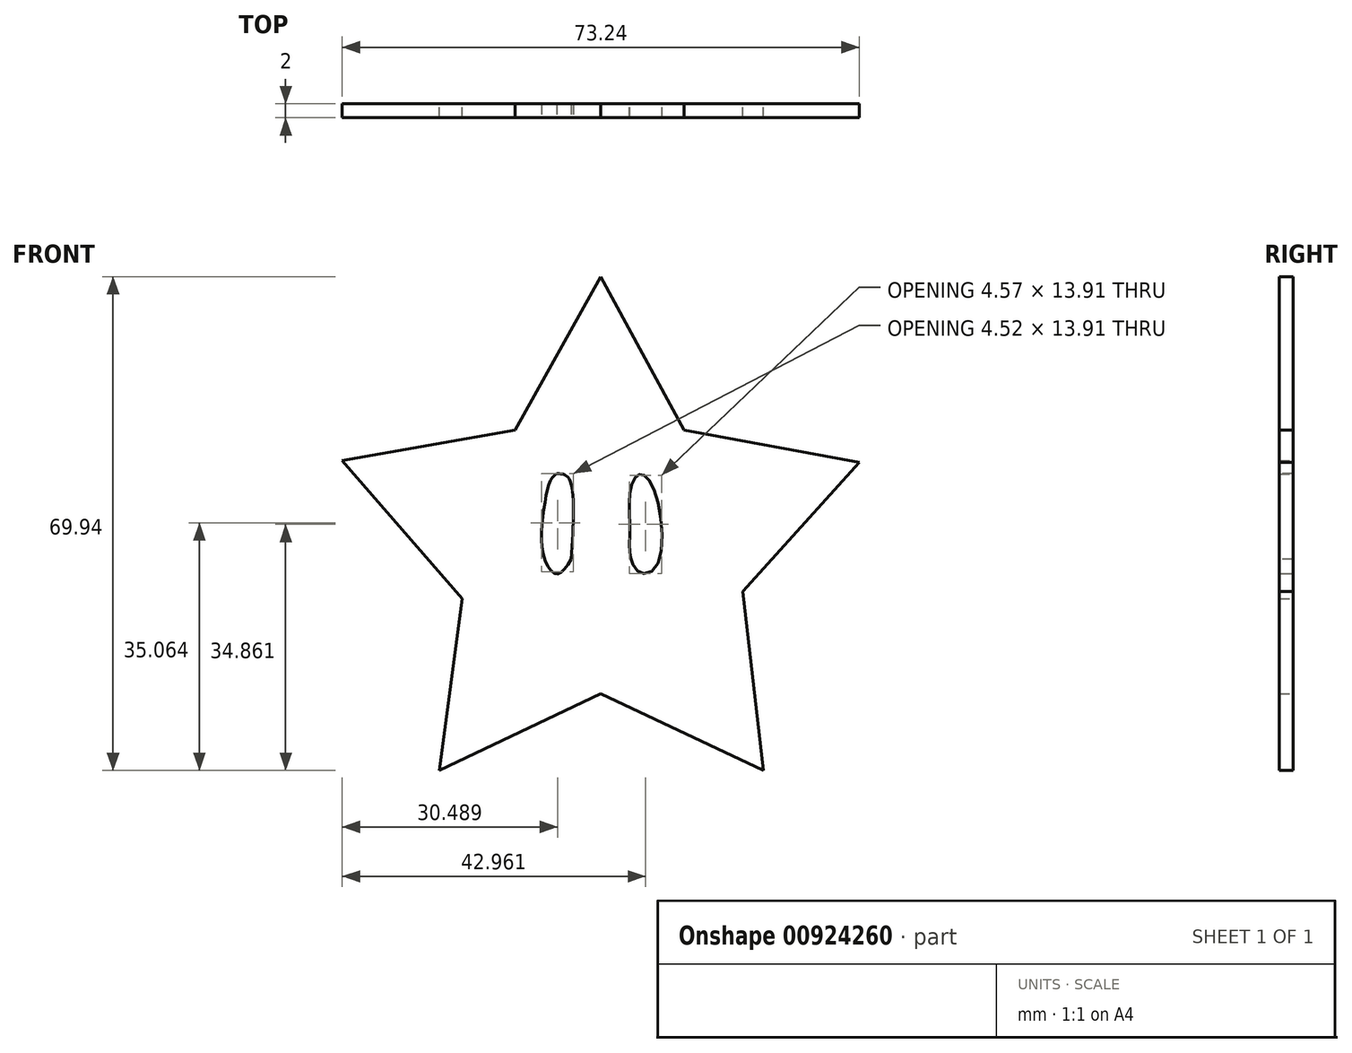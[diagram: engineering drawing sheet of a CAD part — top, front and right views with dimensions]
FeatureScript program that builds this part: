
annotation { "Feature Type Name" : "Feature", "Feature Type Description" : "" }
export const myFeature = defineFeature(function(context is Context, id is Id, definition is map)
    precondition{}
    {
        {
            var Q0;
            Q0=qCreatedBy(makeId("Front.planeOp"),FACE);
            var sketch = newSketch(context, id + "F0", { "sketchPlane" : qUnion([Q0])});
            skLineSegment(sketch, "E0", {"start": v(-73.24, 43.9) * mm, "end": v(-48.73, 48.2) * mm});
            skLineSegment(sketch, "E1", {"start": v(-48.73, 48.2) * mm, "end": v(-36.62, 69.94) * mm});
            skLineSegment(sketch, "E2", {"start": v(-36.62, 69.94) * mm, "end": v(-24.84, 48.2) * mm});
            skLineSegment(sketch, "E3", {"start": v(-24.84, 48.2) * mm, "end": v(0, 43.63) * mm});
            skLineSegment(sketch, "E4", {"start": v(0, 43.63) * mm, "end": v(-16.51, 25.37) * mm});
            skLineSegment(sketch, "E5", {"start": v(-16.51, 25.37) * mm, "end": v(-13.56, 0) * mm});
            skLineSegment(sketch, "E6", {"start": v(-13.56, 0) * mm, "end": v(-36.62, 10.87) * mm});
            skLineSegment(sketch, "E7", {"start": v(-59.47, 0) * mm, "end": v(-36.62, 10.87) * mm});
            skLineSegment(sketch, "E8", {"start": v(-59.47, 0) * mm, "end": v(-56.25, 24.3) * mm});
            skLineSegment(sketch, "E9", {"start": v(-56.25, 24.3) * mm, "end": v(-73.24, 43.9) * mm});
            skSolve(sketch);
        }
        {
            var Q0;
            Q0=makeQuery(id+"F0.imprint","IMPRINT",FACE,{"disambiguationData":[TD([[makeQuery(id+"F0.imprint","IMPRINT",EDGE,{"derivedFrom":sQuery(id+"F0.wireOp",EDGE,"E0")}),-1.0]])]});
            extrude(context, id + "F1", {"entities" : qUnion([Q0]), "depth" : 2 * mm, "offsetDistance" : 25.4 * mm});
        }
        {
            var Q0;
            Q0=makeQuery(id+"F1.opExtrude","CAP_FACE",FACE,{"disambiguationData":[OSD([sQuery(id+"F0.wireOp",EDGE,"E0"),sQuery(id+"F0.wireOp",EDGE,"E1"),sQuery(id+"F0.wireOp",EDGE,"E2"),sQuery(id+"F0.wireOp",EDGE,"E3"),sQuery(id+"F0.wireOp",EDGE,"E4"),sQuery(id+"F0.wireOp",EDGE,"E5"),sQuery(id+"F0.wireOp",EDGE,"E6"),sQuery(id+"F0.wireOp",EDGE,"E7"),sQuery(id+"F0.wireOp",EDGE,"E8"),sQuery(id+"F0.wireOp",EDGE,"E9")])],"isStart":false});
            var sketch = newSketch(context, id + "F2", { "sketchPlane" : qUnion([Q0])});
            skFitSpline(sketch, "E10", {"points": [v(-42.82, 42.02) * mm, v(-41.2, 41.47) * mm, v(-40.82, 29.9) * mm], "startDerivative": vector(6.57, -0.03) * mm, "endDerivative": vector(-1.38, -21.1) * mm});
            skFitSpline(sketch, "E11", {"points": [v(-42.82, 42.02) * mm, v(-43.66, 41.2) * mm, v(-44.63, 37.26) * mm, v(-44.7, 30.34) * mm, v(-42.82, 27.82) * mm, v(-40.82, 29.9) * mm], "startDerivative": vector(-7.6, -5.15) * mm, "endDerivative": vector(10.67, 16.83) * mm});
            skFitSpline(sketch, "E12", {"points": [v(-30.47, 41.82) * mm, v(-31.37, 41.82) * mm, v(-32.4, 39.92) * mm, v(-32.54, 35.78) * mm, v(-32.54, 31.57) * mm, v(-32.34, 29.9) * mm, v(-31.11, 28.01) * mm, v(-28.78, 28.86) * mm, v(-28.53, 37.98) * mm, v(-30.47, 41.82) * mm]});
            skSolve(sketch);
        }
        {
            var Q0;
            Q0=makeQuery(id+"F2.imprint","IMPRINT",FACE,{"disambiguationData":[TD([[makeQuery(id+"F2.imprint","IMPRINT",EDGE,{"derivedFrom":sQuery(id+"F2.wireOp",EDGE,"E10")}),-1.0]])]});
            var Q1;
            Q1=makeQuery(id+"F2.imprint","IMPRINT",FACE,{"disambiguationData":[TD([[makeQuery(id+"F2.imprint","IMPRINT",EDGE,{"derivedFrom":sQuery(id+"F2.wireOp",EDGE,"E12")}),1.0]])]});
            extrude(context, id + "F3", {"entities" : qUnion([Q0, Q1]), "operationType" : NewBodyOperationType.REMOVE, "oppositeDirection" : true, "depth" : 25 * mm, "offsetDistance" : 25 * mm});
        }
    });
